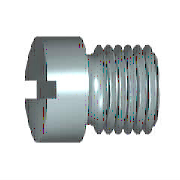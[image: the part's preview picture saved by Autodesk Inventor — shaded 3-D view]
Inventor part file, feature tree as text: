
AUTODESK INVENTOR PART (.ipt)
format: ipt  version: 2020 (Build 240168000, 168)  size: 192,000 bytes
history: native  units: mm (DEFAULTED — no unit token found)
features: other x3, plane x2, extrude x1, fillet x1, sketch x1
ambient origin geometry x7: Origin, YZ Plane, XZ Plane, X Axis, Y Axis, Z Axis, Center Point
bodies: Solid1 (feature_tree)
feature tree (8):
  other  "轴承体"
  plane  "Work Plane1"
  extrude  "开槽"  Depth=0.4mm
  fillet  "圆角1"  Radius=8.0mm
  other  "沟槽1"
  other  "Work Axis1"
  plane  "Work Plane2"
  sketch  "草图2"  dims[d0=10.0mm d1=6.0mm d2=8.0mm d3=9.96mm d4=10.0mm d5=90.0deg d6=-6.0mm d7=1.5mm d8=2.5mm d9=0.0mm d10=6.2mm d11=2.0mm d12=11.2mm d13=10.0mm d14=0.0mm d15=90.0deg d16=90.0deg d18=0.0mm d21=90.0deg d22=0.0mm d23=0.4mm d24=0.0mm]
